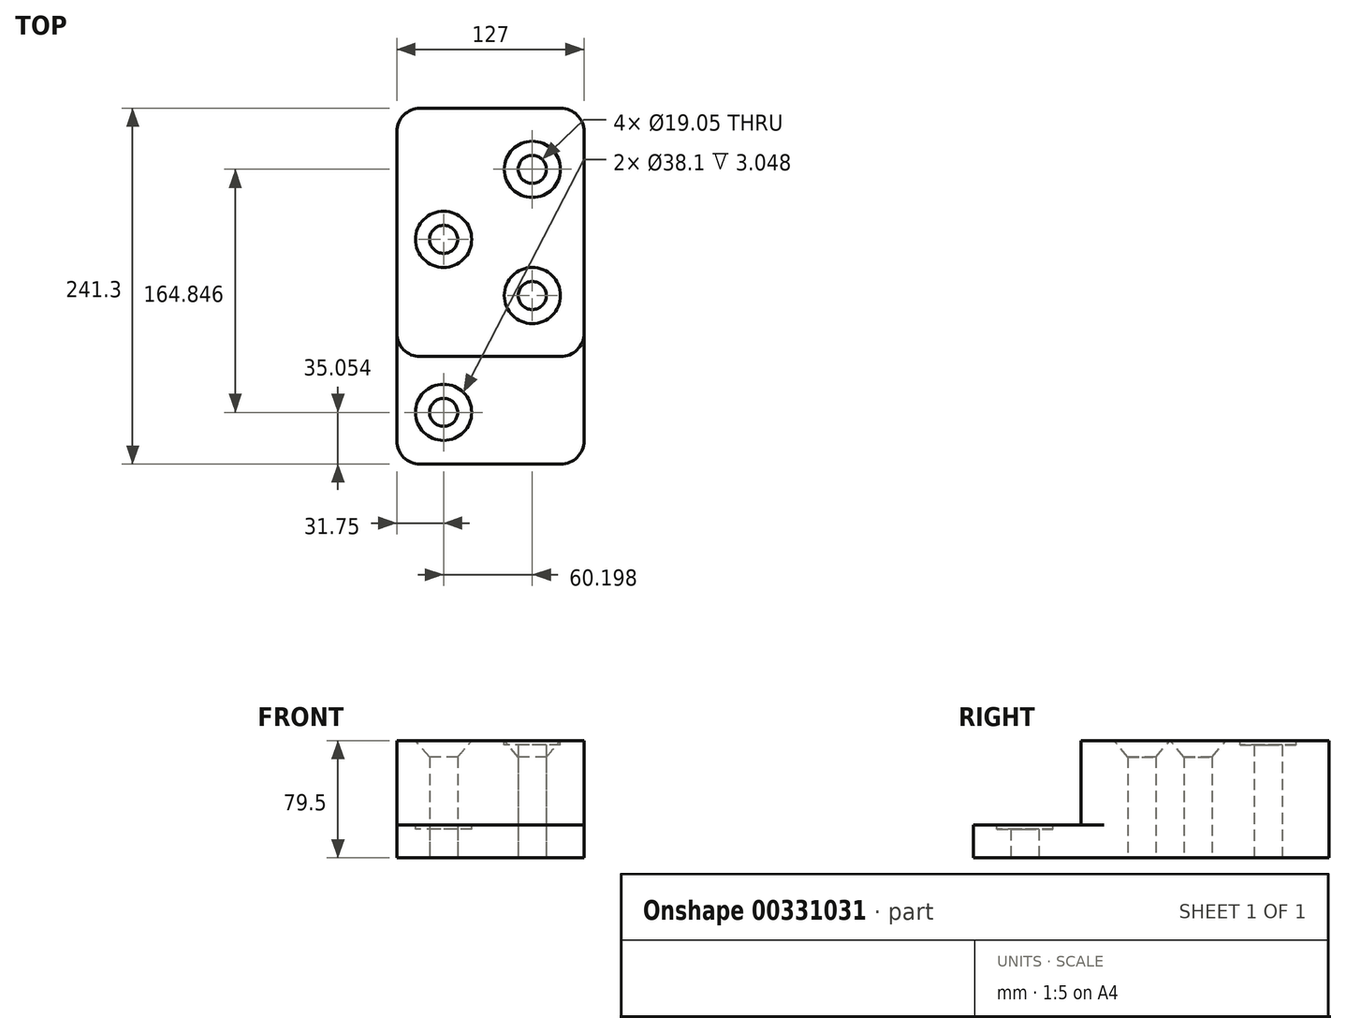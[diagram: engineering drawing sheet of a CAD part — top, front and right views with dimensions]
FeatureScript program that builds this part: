
annotation { "Feature Type Name" : "Feature", "Feature Type Description" : "" }
export const myFeature = defineFeature(function(context is Context, id is Id, definition is map)
    precondition{}
    {
        {
            var Q0;
            Q0=qCreatedBy(makeId("Top.planeOp"),FACE);
            var sketch = newSketch(context, id + "F0", { "sketchPlane" : qUnion([Q0])});
            skLineSegment(sketch, "E0.bottom", {"start": v(0, 0) * mm, "end": v(127, 0) * mm});
            skLineSegment(sketch, "E0.top", {"start": v(0, 168.4) * mm, "end": v(127, 168.4) * mm});
            skLineSegment(sketch, "E0.left", {"start": v(0, 0) * mm, "end": v(0, 168.4) * mm});
            skLineSegment(sketch, "E0.right", {"start": v(127, 0) * mm, "end": v(127, 168.4) * mm});
            skCircle(sketch, "E1", {"center": v(91.95, 127) * mm, "radius": 9.53 * mm});
            skCircle(sketch, "E2", {"center": v(91.95, 41.4) * mm, "radius": 9.53 * mm});
            skCircle(sketch, "E3", {"center": v(31.75, 79.5) * mm, "radius": 9.53 * mm});
            skLineSegment(sketch, "E4.top", {"start": v(0, -72.9) * mm, "end": v(127, -72.9) * mm});
            skLineSegment(sketch, "E4.left", {"start": v(0, 0) * mm, "end": v(0, -72.9) * mm});
            skLineSegment(sketch, "E4.right", {"start": v(127, 0) * mm, "end": v(127, -72.9) * mm});
            skCircle(sketch, "E5", {"center": v(31.75, -37.85) * mm, "radius": 9.53 * mm});
            skSolve(sketch);
        }
        {
            var Q0;
            Q0=makeQuery(id+"F0.imprint","IMPRINT",FACE,{"disambiguationData":[TD([[makeQuery(id+"F0.imprint","IMPRINT",EDGE,{"derivedFrom":sQuery(id+"F0.wireOp",EDGE,"E0.top")}),-1.0]])]});
            extrude(context, id + "F1", {"entities" : qUnion([Q0]), "depth" : 79.5 * mm});
        }
        {
            var Q0;
            Q0=makeQuery(id+"F0.imprint","IMPRINT",FACE,{"disambiguationData":[TD([[makeQuery(id+"F0.imprint","IMPRINT",EDGE,{"derivedFrom":sQuery(id+"F0.wireOp",EDGE,"E0.bottom")}),-1.0]])]});
            extrude(context, id + "F2", {"entities" : qUnion([Q0]), "operationType" : NewBodyOperationType.ADD, "depth" : 22.35 * mm});
        }
        {
            var Q0;
            Q0=makeQuery(id+"F1.opExtrude","CAP_FACE",FACE,{"disambiguationData":[OSD([sQuery(id+"F0.wireOp",EDGE,"E0.top"),sQuery(id+"F0.wireOp",EDGE,"E0.left"),sQuery(id+"F0.wireOp",EDGE,"E0.right"),sQuery(id+"F0.wireOp",EDGE,"E1"),sQuery(id+"F0.wireOp",EDGE,"E2"),sQuery(id+"F0.wireOp",EDGE,"E3"),sQuery(id+"F0.wireOp",EDGE,"E0.bottom")])],"isStart":false});
            var sketch = newSketch(context, id + "F3", { "sketchPlane" : qUnion([Q0])});
            skCircle(sketch, "E6", {"center": v(31.75, 79.5) * mm, "radius": 19.05 * mm});
            skCircle(sketch, "E7", {"center": v(91.95, 127) * mm, "radius": 19.05 * mm});
            skCircle(sketch, "E8", {"center": v(91.95, 41.4) * mm, "radius": 19.05 * mm});
            skSolve(sketch);
        }
        {
            var Q0;
            Q0=makeQuery(id+"F3.imprint","IMPRINT",FACE,{"disambiguationData":[TD([[makeQuery(id+"F3.imprint","IMPRINT",EDGE,{"derivedFrom":sQuery(id+"F3.wireOp",EDGE,"E7")}),1.0]])]});
            extrude(context, id + "F4", {"entities" : qUnion([Q0]), "operationType" : NewBodyOperationType.REMOVE, "oppositeDirection" : true, "depth" : 3.05 * mm});
        }
        {
            var Q0;
            Q0=makeQuery(id+"F1.opExtrude","CAP_FACE",FACE,{"disambiguationData":[OSD([sQuery(id+"F0.wireOp",EDGE,"E0.top"),sQuery(id+"F0.wireOp",EDGE,"E0.left"),sQuery(id+"F0.wireOp",EDGE,"E0.right"),sQuery(id+"F0.wireOp",EDGE,"E1"),sQuery(id+"F0.wireOp",EDGE,"E2"),sQuery(id+"F0.wireOp",EDGE,"E3"),sQuery(id+"F0.wireOp",EDGE,"E0.bottom")])],"isStart":false});
            var sketch = newSketch(context, id + "F5", { "sketchPlane" : qUnion([Q0])});
            skPoint(sketch, "E9", {"position": v(31.75, 79.5) * mm});
            skPoint(sketch, "E10", {"position": v(91.95, 41.4) * mm});
            skSolve(sketch);
        }
        {
            var Q0;
            Q0=sQuery(id+"F5.wireOp",VERTEX,"E9");
            var Q1;
            Q1=sQuery(id+"F5.wireOp",VERTEX,"E10");
            var Q2;
            Q2=makeQuery(id+"F1.opExtrude","SWEPT_BODY",BODY,{"disambiguationData":[OSD([sQuery(id+"F0.wireOp",EDGE,"E0.top"),sQuery(id+"F0.wireOp",EDGE,"E0.left"),sQuery(id+"F0.wireOp",EDGE,"E0.right"),sQuery(id+"F0.wireOp",EDGE,"E1"),sQuery(id+"F0.wireOp",EDGE,"E2"),sQuery(id+"F0.wireOp",EDGE,"E3"),sQuery(id+"F0.wireOp",EDGE,"E0.bottom")])]});
            hole(context, id + "F6", {"style" : HoleStyle.C_SINK, "endStyle" : HoleEndStyle.THROUGH, "holeDiameter" : 19.05 * mm, "cSinkDiameter" : 38.1 * mm, "cSinkAngle" : 81 * degree, "tappedDepth" : 12.7 * mm, "tapClearance" : 3, "locations" : qUnion([Q0, Q1]), "scope" : qUnion([Q2])});
        }
        {
            var Q0;
            Q0=makeQuery(id+"F2.opExtrude","CAP_FACE",FACE,{"disambiguationData":[OSD([sQuery(id+"F0.wireOp",EDGE,"E0.bottom"),sQuery(id+"F0.wireOp",EDGE,"E4.top"),sQuery(id+"F0.wireOp",EDGE,"E4.left"),sQuery(id+"F0.wireOp",EDGE,"E4.right"),sQuery(id+"F0.wireOp",EDGE,"E5")])],"isStart":false});
            var sketch = newSketch(context, id + "F7", { "sketchPlane" : qUnion([Q0])});
            skCircle(sketch, "E11", {"center": v(31.75, -37.85) * mm, "radius": 19.05 * mm});
            skSolve(sketch);
        }
        {
            var Q0;
            Q0 = qSketchRegion(id + "F7", true);
            extrude(context, id + "F8", {"entities" : qUnion([Q0]), "operationType" : NewBodyOperationType.REMOVE, "oppositeDirection" : true, "depth" : 3.05 * mm});
        }
        {
            var Q0;
            Q0=makeQuery(id+"F1.opExtrude","SWEPT_EDGE",EDGE,{"disambiguationData":[OSD([sQuery(id+"F0.wireOp",EDGE,"E0.top"),sQuery(id+"F0.wireOp",EDGE,"E0.left")])]});
            var Q1;
            Q1=makeQuery(id+"F1.opExtrude","SWEPT_EDGE",EDGE,{"disambiguationData":[OSD([sQuery(id+"F0.wireOp",EDGE,"E0.top"),sQuery(id+"F0.wireOp",EDGE,"E0.right")])]});
            var Q2;
            Q2=makeQuery(id+"F1.opExtrude","SWEPT_EDGE",EDGE,{"disambiguationData":[OSD([sQuery(id+"F0.wireOp",EDGE,"E0.right"),sQuery(id+"F0.wireOp",EDGE,"E0.bottom"),sQuery(id+"F0.wireOp",EDGE,"E4.right")])]});
            var Q3;
            Q3=makeQuery(id+"F1.opExtrude","SWEPT_EDGE",EDGE,{"disambiguationData":[OSD([sQuery(id+"F0.wireOp",EDGE,"E0.left"),sQuery(id+"F0.wireOp",EDGE,"E0.bottom"),sQuery(id+"F0.wireOp",EDGE,"E4.left")])]});
            var Q4;
            Q4=makeQuery(id+"F2.opExtrude","SWEPT_EDGE",EDGE,{"disambiguationData":[OSD([sQuery(id+"F0.wireOp",EDGE,"E4.top"),sQuery(id+"F0.wireOp",EDGE,"E4.left")])]});
            var Q5;
            Q5=makeQuery(id+"F2.opExtrude","SWEPT_EDGE",EDGE,{"disambiguationData":[OSD([sQuery(id+"F0.wireOp",EDGE,"E4.top"),sQuery(id+"F0.wireOp",EDGE,"E4.right")])]});
            fillet(context, id + "F9", {"entities" : qUnion([Q0, Q1, Q2, Q3, Q4, Q5]), "radius" : 15.75 * mm, "tangentPropagation" : true, "allowEdgeOverflow" : false});
        }
    });
